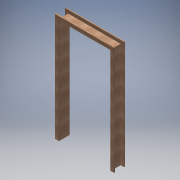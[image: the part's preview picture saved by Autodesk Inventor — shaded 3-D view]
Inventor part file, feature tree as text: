
AUTODESK INVENTOR PART (.ipt)
format: ipt  version: 2017 (Build 210142000, 142)  size: 168,960 bytes
history: native  units: mm
features: extrude x2, sketch x2, chamfer x1, mirror x1, projected_geometry x1
ambient origin geometry x8: Origin, YZ Plane, XZ Plane, XY Plane, X Axis, Y Axis, Z Axis, Center Point
bodies: Volumenkörper1 (feature_tree)
feature tree (7):
  extrude  "Extrusion1"  Depth=950.0mm
  extrude  "Extrusion2"  Depth=60.0mm
  chamfer  "Fase1"  Distance=60.0mm
  mirror  "Spiegeln1"
  sketch  "Skizze1"  dims[d0=1900.0mm d1=950.0mm]
  sketch  "Skizze2"  dims[d2=60.0mm d3=60.0mm d4=60.0mm d5=20.0mm d6=0.0mm d7=15.0mm d8=15.0mm d9=15.0mm d10=950.0mm d11=1900.0mm d12=100.0mm d13=0.0mm d14=5.0mm d15=2.0mm d16=45.0deg]
  projected_geometry  "Projizierte Kontur1"
